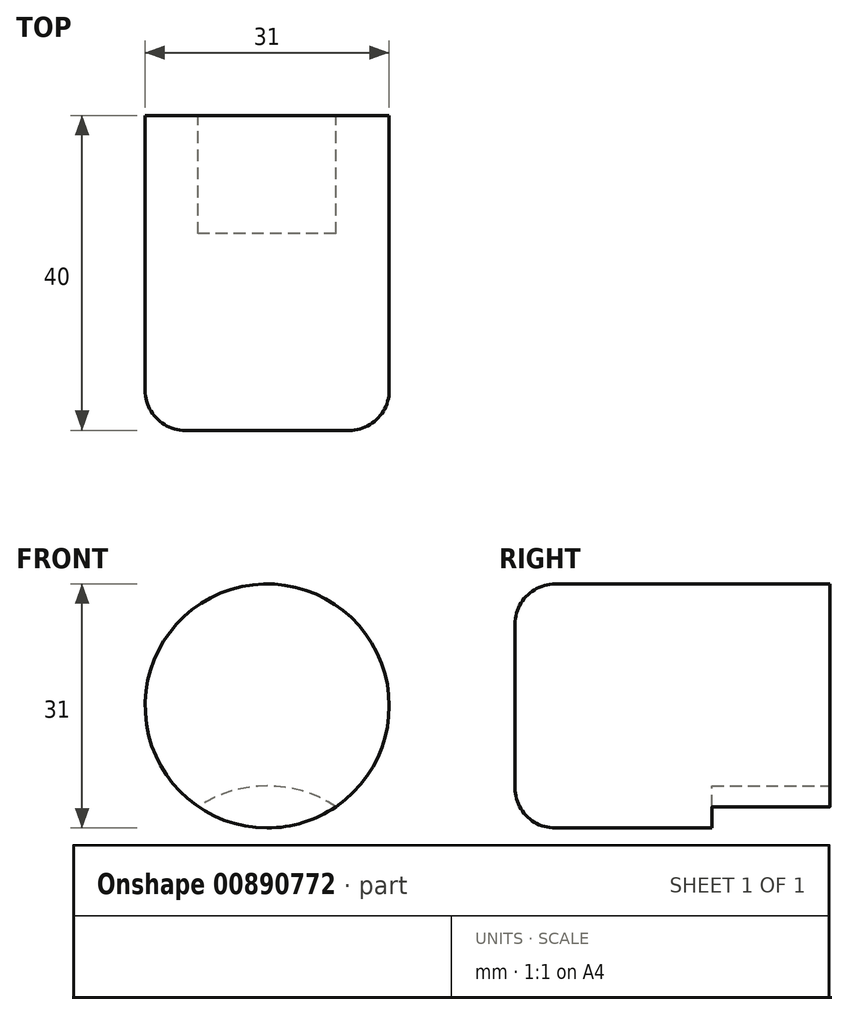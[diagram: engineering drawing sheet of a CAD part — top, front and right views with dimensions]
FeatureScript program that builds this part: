
annotation { "Feature Type Name" : "Feature", "Feature Type Description" : "" }
export const myFeature = defineFeature(function(context is Context, id is Id, definition is map)
    precondition{}
    {
        {
            var Q0;
            Q0=qCreatedBy(makeId("Front.planeOp"),FACE);
            var sketch = newSketch(context, id + "F0", { "sketchPlane" : qUnion([Q0])});
            skCircle(sketch, "E0", {"center": v(-103.9, 18.57) * mm, "radius": 15.5 * mm});
            skArc(sketch, "E1", {"start": v(-95.16, 5.77) * mm, "mid": v(-103.9, 8.4) * mm, "end": v(-112.66, 5.77) * mm});
            skSolve(sketch);
        }
        {
            var Q0;
            {var subQ0=sQuery(id+"F0.wireOp",EDGE,"E1");Q0=makeQuery(id+"F0.imprint","IMPRINT",FACE,{"disambiguationData":[TD([[makeQuery(id+"F0.imprint","IMPRINT",EDGE,{"derivedFrom":subQ0}),-1.0]])]});}
            extrude(context, id + "F1", {"entities" : qUnion([Q0]), "depth" : 15 * mm, "offsetDistance" : 25.4 * mm});
        }
        {
            var Q0;
            Q0=makeQuery(id+"F1.opExtrude","CAP_FACE",FACE,{"disambiguationData":[OSD([sQuery(id+"F0.wireOp",EDGE,"E0"),sQuery(id+"F0.wireOp",EDGE,"E1")])],"isStart":false});
            var sketch = newSketch(context, id + "F2", { "sketchPlane" : qUnion([Q0])});
            skCircle(sketch, "E2", {"center": v(-103.9, 18.57) * mm, "radius": 15.5 * mm});
            skSolve(sketch);
        }
        {
            var Q0;
            Q0 = qSketchRegion(id + "F2", true);
            var Q1;
            {var subQ1=makeQuery(id+"F1.opExtrude","CAP_EDGE",EDGE,{"disambiguationData":[OSD([sQuery(id+"F0.wireOp",EDGE,"E1")])],"isStart":false});Q1=makeQuery(id+"F2.imprint","IMPRINT",FACE,{"disambiguationData":[TD([[makeQuery(id+"F2.imprint","IMPRINT",EDGE,{"derivedFrom":subQ1}),-1.0]])]});}
            extrude(context, id + "F3", {"entities" : qUnion([Q0, Q1]), "operationType" : NewBodyOperationType.ADD, "depth" : 21 * mm, "offsetDistance" : 25.4 * mm});
        }
        {
            var Q0;
            Q0=makeQuery(id+"F3.opExtrude","CAP_FACE",FACE,{"disambiguationData":[OSD([sQuery(id+"F2.wireOp",EDGE,"E2")])],"isStart":false});
            var sketch = newSketch(context, id + "F4", { "sketchPlane" : qUnion([Q0])});
            skCircle(sketch, "E3", {"center": v(-103.9, 18.57) * mm, "radius": 15.5 * mm});
            skSolve(sketch);
        }
        {
            var Q0;
            Q0=makeQuery(id+"F4.imprint","IMPRINT",FACE,{"disambiguationData":[TD([[makeQuery(id+"F4.imprint","IMPRINT",EDGE,{"derivedFrom":sQuery(id+"F4.wireOp",EDGE,"E3")}),1.0]])]});
            extrude(context, id + "F5", {"entities" : qUnion([Q0]), "operationType" : NewBodyOperationType.ADD, "depth" : 4 * mm, "offsetDistance" : 25.4 * mm});
        }
        {
            var Q0;
            Q0=makeQuery(id+"F5.opExtrude","CAP_EDGE",EDGE,{"disambiguationData":[OSD([sQuery(id+"F4.wireOp",EDGE,"E3")])],"isStart":false});
            fillet(context, id + "F6", {"entities" : qUnion([Q0]), "radius" : 5.08 * mm, "tangentPropagation" : true, "allowEdgeOverflow" : false});
        }
    });
